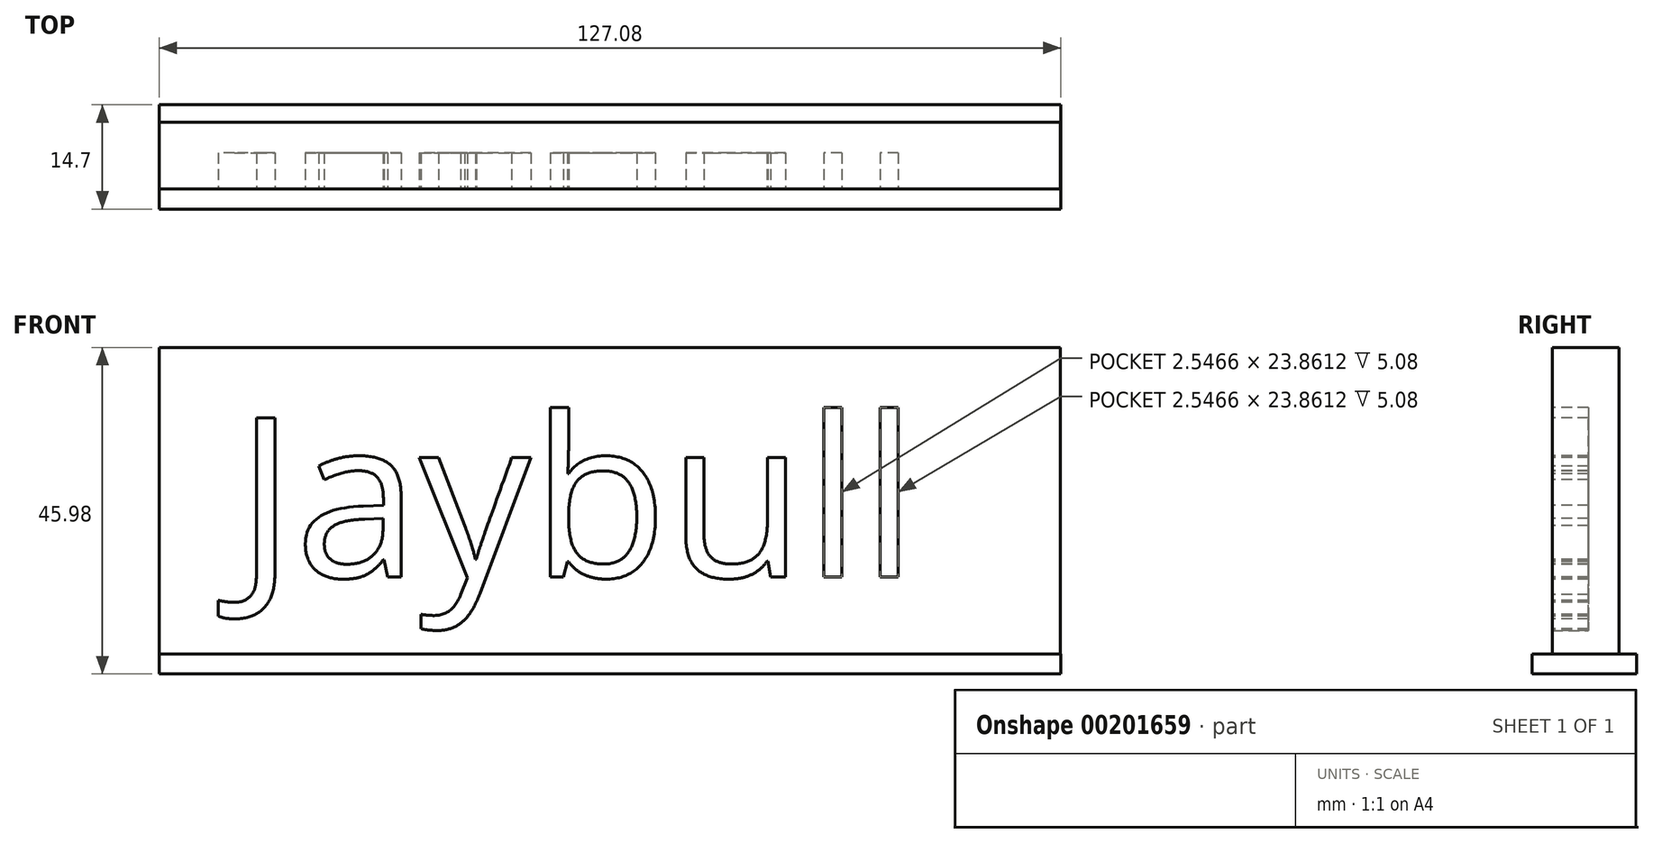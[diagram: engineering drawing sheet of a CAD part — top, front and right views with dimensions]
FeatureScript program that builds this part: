
annotation { "Feature Type Name" : "Feature", "Feature Type Description" : "" }
export const myFeature = defineFeature(function(context is Context, id is Id, definition is map)
    precondition{}
    {
        {
            var Q0;
            Q0=qCreatedBy(makeId("Front.planeOp"),FACE);
            var sketch = newSketch(context, id + "F0", { "sketchPlane" : qUnion([Q0])});
            skLineSegment(sketch, "E0.bottom", {"start": v(-50.16, 29) * mm, "end": v(76.84, 29) * mm});
            skLineSegment(sketch, "E0.top", {"start": v(-50.16, -14.17) * mm, "end": v(76.84, -14.17) * mm});
            skLineSegment(sketch, "E0.left", {"start": v(-50.16, 29) * mm, "end": v(-50.16, -14.17) * mm});
            skLineSegment(sketch, "E0.right", {"start": v(76.84, 29) * mm, "end": v(76.84, -14.17) * mm});
            skSolve(sketch);
        }
        {
            var Q0;
            Q0=makeQuery(id+"F0.imprint","IMPRINT",FACE,{"disambiguationData":[TD([[makeQuery(id+"F0.imprint","IMPRINT",EDGE,{"derivedFrom":sQuery(id+"F0.wireOp",EDGE,"E0.bottom")}),-1.0]])]});
            extrude(context, id + "F1", {"entities" : qUnion([Q0]), "depth" : 9.4 * mm});
        }
        {
            var Q0;
            Q0=makeQuery(id+"F1.opExtrude","CAP_FACE",FACE,{"disambiguationData":[OSD([sQuery(id+"F0.wireOp",EDGE,"E0.bottom"),sQuery(id+"F0.wireOp",EDGE,"E0.top"),sQuery(id+"F0.wireOp",EDGE,"E0.left"),sQuery(id+"F0.wireOp",EDGE,"E0.right")])],"isStart":false});
            var sketch = newSketch(context, id + "F2", { "sketchPlane" : qUnion([Q0])});
            skText(sketch, "E1", { "text": "Jaybull", "fontName": "OpenSans-Regular.ttf"});
            const initialGuessF2  = {"E1": [-0.03937, -0.00333, 1, 0, 0.02261]};
            skSetInitialGuess(sketch, initialGuessF2);
            skSolve(sketch);
        }
        {
            var Q0;
            Q0 = qSketchRegion(id + "F2", true);
            extrude(context, id + "F3", {"entities" : qUnion([Q0]), "operationType" : NewBodyOperationType.REMOVE, "oppositeDirection" : true, "depth" : 5.08 * mm});
        }
        {
            var Q0;
            Q0=makeQuery(id+"F1.opExtrude","SWEPT_FACE",FACE,{"disambiguationData":[OSD([sQuery(id+"F0.wireOp",EDGE,"E0.top")])]});
            var sketch = newSketch(context, id + "F4", { "sketchPlane" : qUnion([Q0])});
            skLineSegment(sketch, "E2.bottom", {"start": v(-50.16, -2.48) * mm, "end": v(76.92, -2.48) * mm});
            skLineSegment(sketch, "E2.top", {"start": v(-50.16, 12.22) * mm, "end": v(76.92, 12.22) * mm});
            skLineSegment(sketch, "E2.left", {"start": v(-50.16, -2.48) * mm, "end": v(-50.16, 12.22) * mm});
            skLineSegment(sketch, "E2.right", {"start": v(76.92, -2.48) * mm, "end": v(76.92, 12.22) * mm});
            skSolve(sketch);
        }
        {
            var Q0;
            {var subQ5=sQuery(id+"F4.wireOp",EDGE,"E2.bottom");Q0=makeQuery(id+"F4.imprint","IMPRINT",FACE,{"disambiguationData":[TD([[makeQuery(id+"F4.imprint","IMPRINT",EDGE,{"derivedFrom":subQ5}),1.0]])]});}
            var Q1;
            {var subQ1=sQuery(id+"F0.wireOp",EDGE,"E0.top");var subQ2=makeQuery(id+"F1.opExtrude","CAP_EDGE",EDGE,{"disambiguationData":[OSD([subQ1])],"isStart":true});Q1=makeQuery(id+"F4.imprint","IMPRINT",FACE,{"disambiguationData":[TD([[makeQuery(id+"F4.imprint","IMPRINT",EDGE,{"derivedFrom":subQ2}),1.0]])]});}
            extrude(context, id + "F5", {"entities" : qUnion([Q0, Q1]), "operationType" : NewBodyOperationType.ADD, "depth" : 2.8 * mm});
        }
    });
